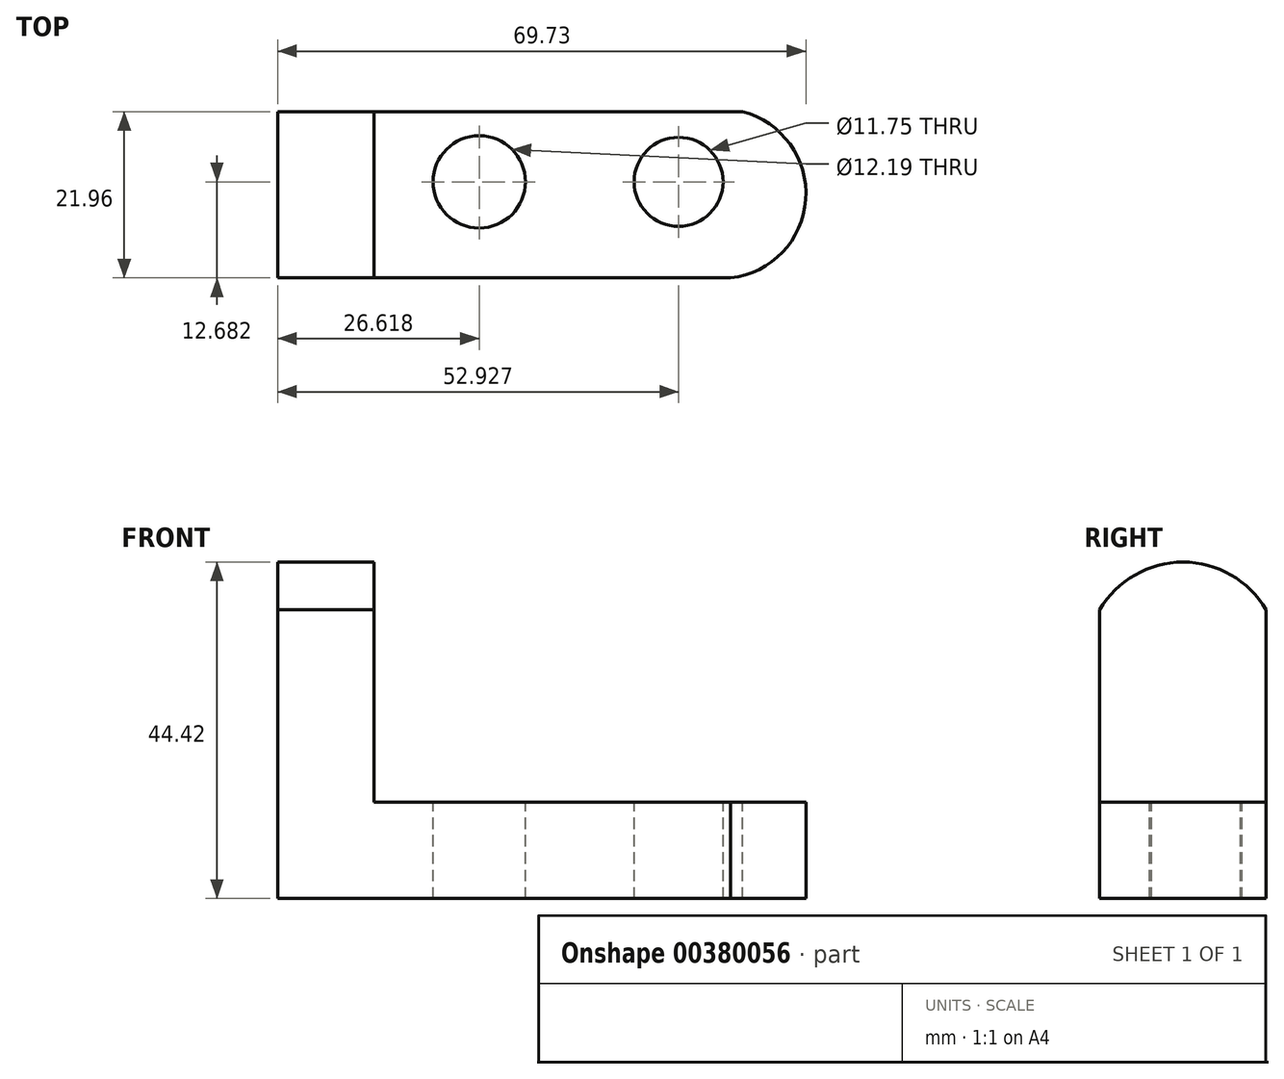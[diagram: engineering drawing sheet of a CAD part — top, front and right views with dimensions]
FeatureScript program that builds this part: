
annotation { "Feature Type Name" : "Feature", "Feature Type Description" : "" }
export const myFeature = defineFeature(function(context is Context, id is Id, definition is map)
    precondition{}
    {
        {
            var Q0;
            Q0=qCreatedBy(makeId("Front.planeOp"),FACE);
            var sketch = newSketch(context, id + "F0", { "sketchPlane" : qUnion([Q0])});
            skLineSegment(sketch, "E0", {"start": v(0, 0) * mm, "end": v(0, 38.1) * mm});
            skLineSegment(sketch, "E1", {"start": v(0, 38.1) * mm, "end": v(69.85, 38.1) * mm});
            skLineSegment(sketch, "E2", {"start": v(69.85, 38.1) * mm, "end": v(69.85, 0) * mm});
            skLineSegment(sketch, "E3", {"start": v(69.85, 0) * mm, "end": v(0, 0) * mm});
            skSolve(sketch);
        }
        {
            var Q0;
            Q0=makeQuery(id+"F0.imprint","IMPRINT",FACE,{"disambiguationData":[TD([[makeQuery(id+"F0.imprint","IMPRINT",EDGE,{"derivedFrom":sQuery(id+"F0.wireOp",EDGE,"E0")}),-1.0]])]});
            extrude(context, id + "F1", {"entities" : qUnion([Q0]), "depth" : 25.4 * mm});
        }
        {
            var Q0;
            Q0=makeQuery(id+"F1.opExtrude","SWEPT_FACE",FACE,{"disambiguationData":[OSD([sQuery(id+"F0.wireOp",EDGE,"E2")])]});
            var sketch = newSketch(context, id + "F2", { "sketchPlane" : qUnion([Q0])});
            skCircle(sketch, "E4", {"center": v(-12.7, 31.73) * mm, "radius": 12.7 * mm});
            skSolve(sketch);
        }
        {
            var Q0;
            {var subQ0=sQuery(id+"F2.wireOp",EDGE,"E4");var subQ1=makeQuery(id+"F1.opExtrude","SWEPT_EDGE",EDGE,{"disambiguationData":[OSD([sQuery(id+"F0.wireOp",EDGE,"E1"),sQuery(id+"F0.wireOp",EDGE,"E2")])]});var subQ2=makeQuery(id+"F2.imprint","INTERSECT",VERTEX,{"disambiguationData":[OD(0.0)],"derivedFrom":[subQ1,subQ0]});Q0=makeQuery(id+"F2.imprint","IMPRINT",FACE,{"disambiguationData":[TD([[makeQuery(id+"F2.imprint","IMPRINT",EDGE,{"disambiguationData":[TD([[subQ2,-1.0]])],"derivedFrom":subQ0}),1.0]])]});}
            extrude(context, id + "F3", {"entities" : qUnion([Q0]), "operationType" : NewBodyOperationType.ADD, "oppositeDirection" : true, "depth" : 69.85 * mm});
        }
        {
            var Q0;
            {var subQ1=sQuery(id+"F0.wireOp",EDGE,"E2");var subQ2=sQuery(id+"F0.wireOp",EDGE,"E1");var subQ3=sQuery(id+"F0.wireOp",EDGE,"E0");Q0=makeQuery(id+"F3.boolean.opBoolean","SPLIT",FACE,{"disambiguationData":[TD([makeQuery(id+"F1.opExtrude","CAP_FACE",FACE,{"disambiguationData":[OSD([subQ3,subQ2,subQ1,sQuery(id+"F0.wireOp",EDGE,"E3")])],"isStart":true})])],"derivedFrom":makeQuery(id+"F1.opExtrude","SWEPT_FACE",FACE,{"disambiguationData":[OSD([subQ2])]})});}
            extrude(context, id + "F4", {"entities" : qUnion([Q0]), "operationType" : NewBodyOperationType.REMOVE, "oppositeDirection" : true, "depth" : 50.8 * mm});
        }
        {
            var Q0;
            {var subQ1=sQuery(id+"F0.wireOp",EDGE,"E2");var subQ2=sQuery(id+"F0.wireOp",EDGE,"E1");var subQ3=sQuery(id+"F0.wireOp",EDGE,"E0");Q0=makeQuery(id+"F3.boolean.opBoolean","SPLIT",FACE,{"disambiguationData":[TD([makeQuery(id+"F1.opExtrude","CAP_FACE",FACE,{"disambiguationData":[OSD([subQ3,subQ2,subQ1,sQuery(id+"F0.wireOp",EDGE,"E3")])],"isStart":false})])],"derivedFrom":makeQuery(id+"F1.opExtrude","SWEPT_FACE",FACE,{"disambiguationData":[OSD([subQ2])]})});}
            extrude(context, id + "F5", {"entities" : qUnion([Q0]), "operationType" : NewBodyOperationType.REMOVE, "oppositeDirection" : true, "depth" : 50.8 * mm});
        }
        {
            var Q0;
            Q0=makeQuery(id+"F5.boolean.opBoolean","COPY",FACE,{"derivedFrom":makeQuery(id+"F5.opExtrude","SWEPT_FACE",FACE,{"disambiguationData":[OSD([sQuery(id+"F0.wireOp",EDGE,"E1"),sQuery(id+"F0.wireOp",EDGE,"E2"),sQuery(id+"F2.wireOp",EDGE,"E4")])]})});
            var sketch = newSketch(context, id + "F6", { "sketchPlane" : qUnion([Q0])});
            skLineSegment(sketch, "E5", {"start": v(12.7, 38.1) * mm, "end": v(12.7, 12.7) * mm});
            skLineSegment(sketch, "E6", {"start": v(12.7, 12.7) * mm, "end": v(69.85, 12.7) * mm});
            skSolve(sketch);
        }
        {
            var Q0;
            {var subQ0=sQuery(id+"F6.wireOp",EDGE,"E5");Q0=makeQuery(id+"F6.imprint","IMPRINT",FACE,{"disambiguationData":[TD([[makeQuery(id+"F6.imprint","IMPRINT",EDGE,{"derivedFrom":subQ0}),1.0]])]});}
            extrude(context, id + "F7", {"entities" : qUnion([Q0]), "operationType" : NewBodyOperationType.REMOVE, "oppositeDirection" : true, "depth" : 25.4 * mm});
        }
        {
            var Q0;
            {var subQ0=sQuery(id+"F2.wireOp",EDGE,"E4");var subQ1=sQuery(id+"F0.wireOp",EDGE,"E2");var subQ2=sQuery(id+"F0.wireOp",EDGE,"E1");Q0=makeQuery(id+"F7.boolean.opBoolean","SPLIT",FACE,{"disambiguationData":[TD([makeQuery(id+"F3.opExtrude","SWEPT_FACE",FACE,{"disambiguationData":[OSD([subQ0])]})])],"derivedFrom":makeQuery(id+"F3.boolean.opBoolean","MERGE",FACE,{"derivedFrom":[makeQuery(id+"F1.opExtrude","SWEPT_FACE",FACE,{"disambiguationData":[OSD([subQ1])]}),makeQuery(id+"F3.opExtrude","CAP_FACE",FACE,{"disambiguationData":[OSD([subQ2,subQ1,subQ0])],"isStart":true})]})});}
            extrude(context, id + "F8", {"entities" : qUnion([Q0]), "operationType" : NewBodyOperationType.REMOVE, "oppositeDirection" : true, "depth" : 25.4 * mm});
        }
        {
            var Q0;
            Q0=makeQuery(id+"F8.boolean.opBoolean","COPY",FACE,{"derivedFrom":makeQuery(id+"F8.opExtrude","CAP_FACE",FACE,{"disambiguationData":[OSD([sQuery(id+"F0.wireOp",EDGE,"E1"),sQuery(id+"F0.wireOp",EDGE,"E2"),sQuery(id+"F2.wireOp",EDGE,"E4")])],"isStart":false})});
            extrude(context, id + "F9", {"entities" : qUnion([Q0]), "operationType" : NewBodyOperationType.REMOVE, "oppositeDirection" : true, "depth" : 31.75 * mm});
        }
        {
            var Q0;
            Q0=makeQuery(id+"F7.boolean.opBoolean","COPY",FACE,{"derivedFrom":makeQuery(id+"F7.opExtrude","SWEPT_FACE",FACE,{"disambiguationData":[OSD([sQuery(id+"F6.wireOp",EDGE,"E6")])]})});
            var sketch = newSketch(context, id + "F10", { "sketchPlane" : qUnion([Q0])});
            skArc(sketch, "E7", {"start": v(57.26, -23.67) * mm, "mid": v(69.7, -11.76) * mm, "end": v(55.71, -1.71) * mm});
            skSolve(sketch);
        }
        {
            var Q0;
            {var subQ1=sQuery(id+"F6.wireOp",EDGE,"E6");var subQ4=sQuery(id+"F2.wireOp",EDGE,"E4");var subQ5=sQuery(id+"F0.wireOp",EDGE,"E2");var subQ6=sQuery(id+"F0.wireOp",EDGE,"E1");var subQ9=makeQuery(id+"F7.boolean.opBoolean","COPY",EDGE,{"derivedFrom":makeQuery(id+"F7.opExtrude","SWEPT_EDGE",EDGE,{"disambiguationData":[OSD([subQ6,subQ5,subQ4,subQ1])]})});Q0=makeQuery(id+"F10.imprint","IMPRINT",FACE,{"disambiguationData":[TD([[makeQuery(id+"F10.imprint","IMPRINT",EDGE,{"derivedFrom":subQ9}),-1.0]])]});}
            extrude(context, id + "F11", {"entities" : qUnion([Q0]), "operationType" : NewBodyOperationType.REMOVE, "oppositeDirection" : true, "depth" : 25.4 * mm});
        }
        {
            var Q0;
            Q0=makeQuery(id+"F7.boolean.opBoolean","COPY",FACE,{"derivedFrom":makeQuery(id+"F7.opExtrude","SWEPT_FACE",FACE,{"disambiguationData":[OSD([sQuery(id+"F6.wireOp",EDGE,"E6")])]})});
            var sketch = newSketch(context, id + "F12", { "sketchPlane" : qUnion([Q0])});
            skCircle(sketch, "E8", {"center": v(26.62, -10.99) * mm, "radius": 6.1 * mm});
            skCircle(sketch, "E9", {"center": v(52.93, -10.99) * mm, "radius": 5.87 * mm});
            skSolve(sketch);
        }
        {
            var Q0;
            Q0=makeQuery(id+"F12.imprint","IMPRINT",FACE,{"disambiguationData":[TD([[makeQuery(id+"F12.imprint","IMPRINT",EDGE,{"derivedFrom":sQuery(id+"F12.wireOp",EDGE,"E8")}),1.0]])]});
            var Q1;
            Q1=makeQuery(id+"F12.imprint","IMPRINT",FACE,{"disambiguationData":[TD([[makeQuery(id+"F12.imprint","IMPRINT",EDGE,{"derivedFrom":sQuery(id+"F12.wireOp",EDGE,"E9")}),1.0]])]});
            var Q2;
            Q2=sQuery(id+"F12.wireOp",EDGE,"E8");
            var Q3;
            Q3=sQuery(id+"F12.wireOp",EDGE,"E9");
            extrude(context, id + "F13", {"entities" : qUnion([Q0, Q1]), "operationType" : NewBodyOperationType.REMOVE, "surfaceEntities" : qUnion([Q2, Q3]), "oppositeDirection" : true, "depth" : 25.4 * mm});
        }
        {
            var Q0;
            Q0=makeQuery(id+"F9.boolean.opBoolean","MERGE",FACE,{"derivedFrom":[makeQuery(id+"F7.boolean.opBoolean","COPY",FACE,{"derivedFrom":makeQuery(id+"F7.opExtrude","SWEPT_FACE",FACE,{"disambiguationData":[OSD([sQuery(id+"F6.wireOp",EDGE,"E5")])]})}),makeQuery(id+"F9.opExtrude","CAP_FACE",FACE,{"disambiguationData":[OSD([sQuery(id+"F0.wireOp",EDGE,"E1"),sQuery(id+"F0.wireOp",EDGE,"E2"),sQuery(id+"F2.wireOp",EDGE,"E4")])],"isStart":false})]});
            var sketch = newSketch(context, id + "F14", { "sketchPlane" : qUnion([Q0])});
            skCircle(sketch, "E10", {"center": v(-13, 38.1) * mm, "radius": 8.07 * mm});
            skSolve(sketch);
        }
        {
            var Q0;
            {var subQ0=sQuery(id+"F14.wireOp",EDGE,"E10");var subQ1=makeQuery(id+"F9.boolean.opBoolean","COPY",EDGE,{"derivedFrom":makeQuery(id+"F9.opExtrude","CAP_EDGE",EDGE,{"disambiguationData":[OSD([sQuery(id+"F2.wireOp",EDGE,"E4")])],"isStart":false})});var subQ2=makeQuery(id+"F14.imprint","INTERSECT",VERTEX,{"disambiguationData":[OD(0.0)],"derivedFrom":[subQ1,subQ0]});Q0=makeQuery(id+"F14.imprint","IMPRINT",FACE,{"disambiguationData":[TD([[makeQuery(id+"F14.imprint","IMPRINT",EDGE,{"disambiguationData":[TD([[subQ2,-1.0]])],"derivedFrom":subQ0}),1.0]])]});}
            extrude(context, id + "F15", {"entities" : qUnion([Q0]), "operationType" : NewBodyOperationType.REMOVE, "oppositeDirection" : true, "depth" : 25.4 * mm});
        }
    });
